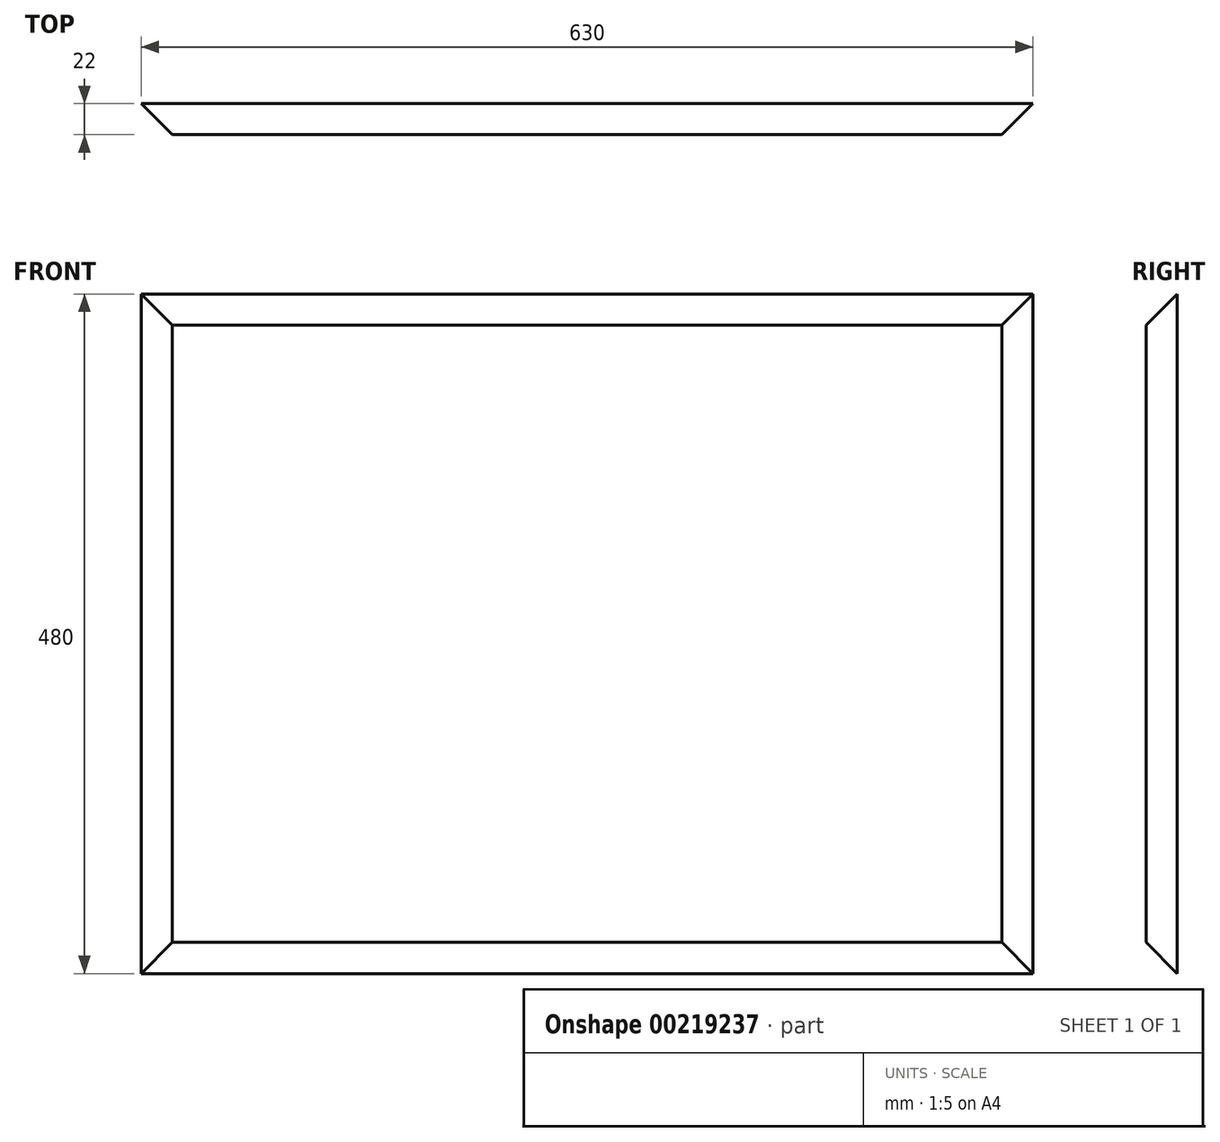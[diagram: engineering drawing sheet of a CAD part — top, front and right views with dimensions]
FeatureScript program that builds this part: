
annotation { "Feature Type Name" : "Feature", "Feature Type Description" : "" }
export const myFeature = defineFeature(function(context is Context, id is Id, definition is map)
    precondition{}
    {
        {
            var Q0;
            Q0=qCreatedBy(makeId("Front.planeOp"),FACE);
            var sketch = newSketch(context, id + "F0", { "sketchPlane" : qUnion([Q0])});
            skLineSegment(sketch, "E0.bottom", {"start": v(-315, 240) * mm, "end": v(315, 240) * mm});
            skLineSegment(sketch, "E0.top", {"start": v(-315, -240) * mm, "end": v(315, -240) * mm});
            skLineSegment(sketch, "E0.left", {"start": v(-315, 240) * mm, "end": v(-315, -240) * mm});
            skLineSegment(sketch, "E0.right", {"start": v(315, 240) * mm, "end": v(315, -240) * mm});
            skPoint(sketch, "E0.middle", {"position": v(0, 0) * mm});
            skSolve(sketch);
        }
        {
            var Q0;
            Q0=makeQuery(id+"F0.imprint","IMPRINT",FACE,{"disambiguationData":[TD([[makeQuery(id+"F0.imprint","IMPRINT",EDGE,{"derivedFrom":sQuery(id+"F0.wireOp",EDGE,"E0.bottom")}),-1.0]])]});
            extrude(context, id + "F1", {"entities" : qUnion([Q0]), "depth" : 22 * mm});
        }
        {
            var Q0;
            Q0=makeQuery(id+"F1.opExtrude","CAP_EDGE",EDGE,{"disambiguationData":[OSD([sQuery(id+"F0.wireOp",EDGE,"E0.left")])],"isStart":false});
            var Q1;
            Q1=makeQuery(id+"F1.opExtrude","CAP_EDGE",EDGE,{"disambiguationData":[OSD([sQuery(id+"F0.wireOp",EDGE,"E0.bottom")])],"isStart":false});
            var Q2;
            Q2=makeQuery(id+"F1.opExtrude","CAP_EDGE",EDGE,{"disambiguationData":[OSD([sQuery(id+"F0.wireOp",EDGE,"E0.right")])],"isStart":false});
            var Q3;
            Q3=makeQuery(id+"F1.opExtrude","CAP_EDGE",EDGE,{"disambiguationData":[OSD([sQuery(id+"F0.wireOp",EDGE,"E0.top")])],"isStart":false});
            chamfer(context, id + "F2", {"entities" : qUnion([Q0, Q1, Q2, Q3]), "width" : 22 * mm, "tangentPropagation" : true});
        }
    });
